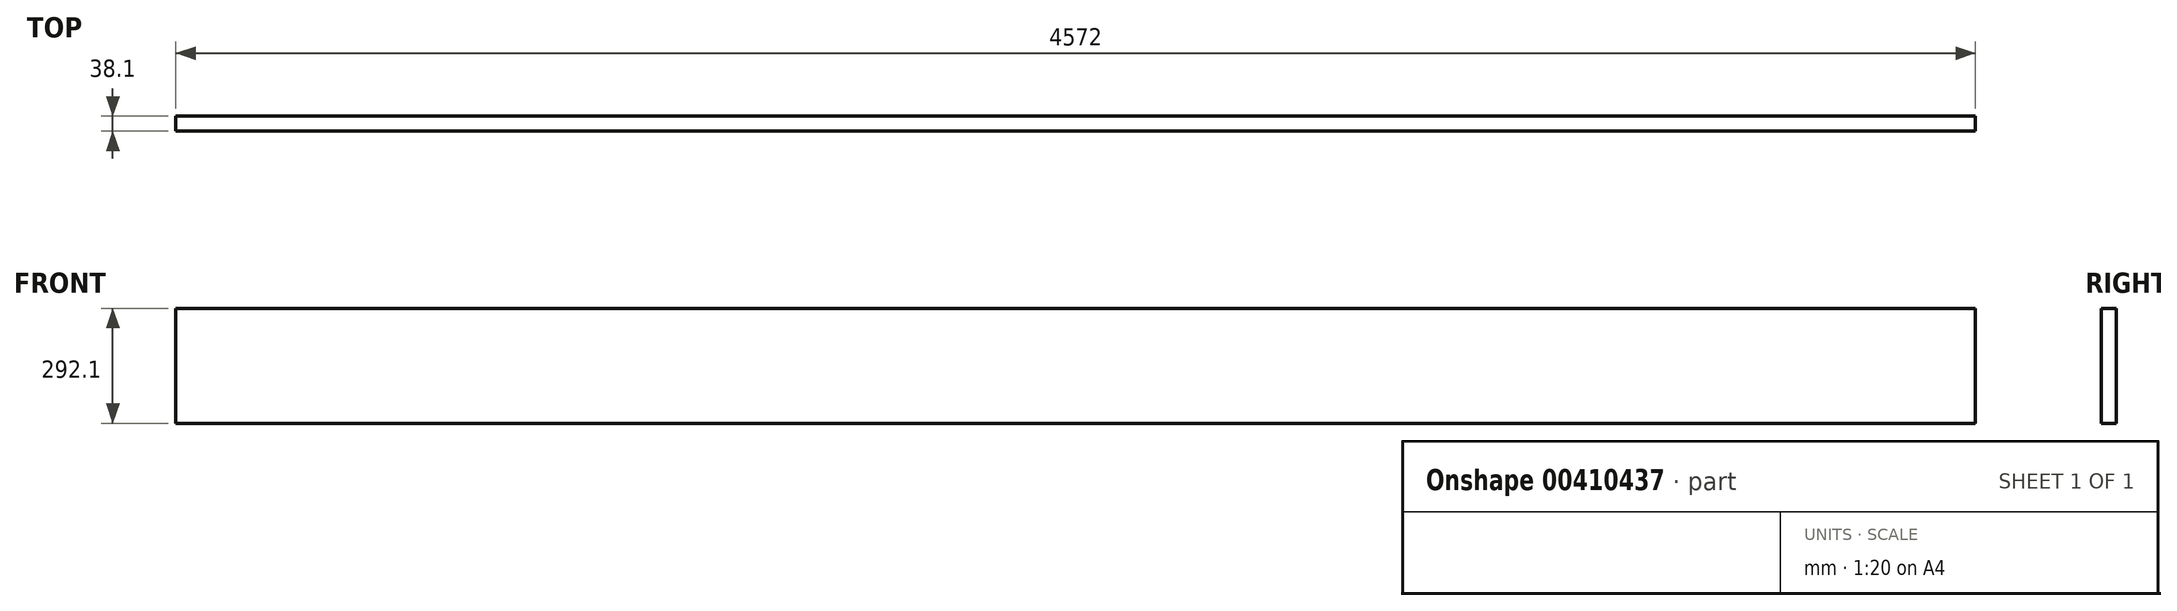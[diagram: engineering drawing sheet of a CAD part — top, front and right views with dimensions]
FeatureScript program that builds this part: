
annotation { "Feature Type Name" : "Feature", "Feature Type Description" : "" }
export const myFeature = defineFeature(function(context is Context, id is Id, definition is map)
    precondition{}
    {
        {
            var Q0;
            Q0=qCreatedBy(makeId("Front.planeOp"),FACE);
            var sketch = newSketch(context, id + "F0", { "sketchPlane" : qUnion([Q0])});
            skLineSegment(sketch, "E0.bottom", {"start": v(-2286, 146.05) * mm, "end": v(2286, 146.05) * mm});
            skLineSegment(sketch, "E0.top", {"start": v(-2286, -146.05) * mm, "end": v(2286, -146.05) * mm});
            skLineSegment(sketch, "E0.left", {"start": v(-2286, 146.05) * mm, "end": v(-2286, -146.05) * mm});
            skLineSegment(sketch, "E0.right", {"start": v(2286, 146.05) * mm, "end": v(2286, -146.05) * mm});
            skPoint(sketch, "E0.middle", {"position": v(0, 0) * mm});
            skSolve(sketch);
        }
        {
            var Q0;
            Q0=qSketchRegion(id+"F0",true);
            extrude(context, id + "F1", {"entities" : qUnion([Q0]), "depth" : 38.1 * mm, "offsetDistance" : 25.4 * mm});
        }
    });
